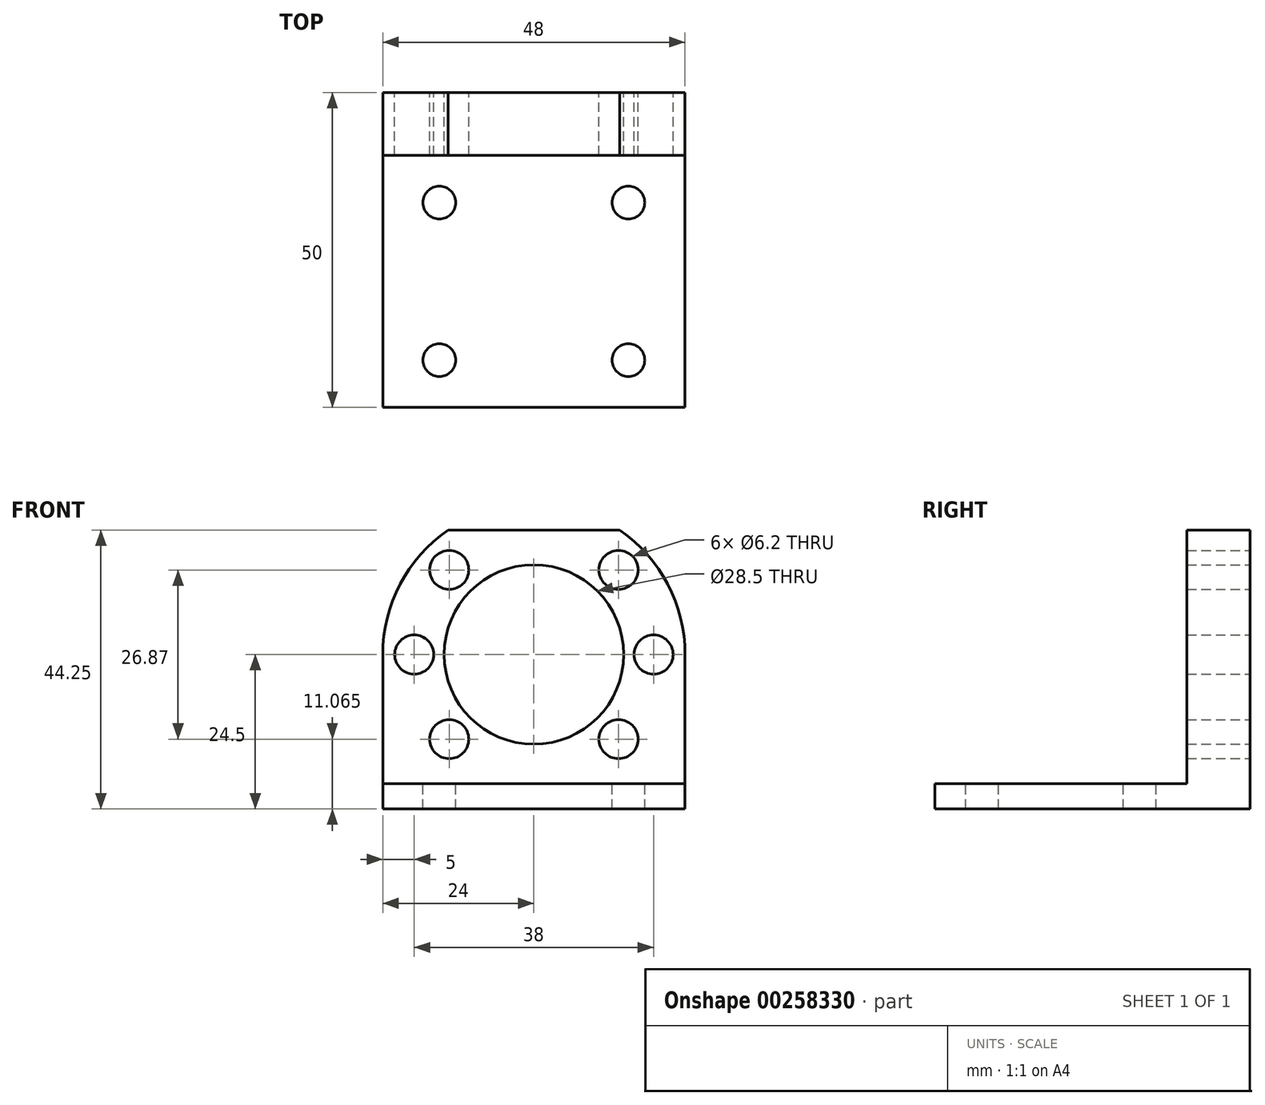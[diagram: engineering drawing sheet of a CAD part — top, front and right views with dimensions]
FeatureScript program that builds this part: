
annotation { "Feature Type Name" : "Feature", "Feature Type Description" : "" }
export const myFeature = defineFeature(function(context is Context, id is Id, definition is map)
    precondition{}
    {
        {
            var Q0;
            Q0=qCreatedBy(makeId("Front.planeOp"),FACE);
            var sketch = newSketch(context, id + "F0", { "sketchPlane" : qUnion([Q0])});
            skCircle(sketch, "E0", {"center": v(0, 0) * mm, "radius": 14.25 * mm});
            skArc(sketch, "E1", {"start": v(-13.64, 19.75) * mm, "mid": v(-21.25, 11.15) * mm, "end": v(-24, 0) * mm});
            skLineSegment(sketch, "E2", {"start": v(-13.64, 19.75) * mm, "end": v(13.64, 19.75) * mm});
            skLineSegment(sketch, "E3", {"start": v(24, 0) * mm, "end": v(-24, 0) * mm, "construction": true});
            skCircle(sketch, "E4", {"center": v(0, 0) * mm, "radius": 19 * mm, "construction": true});
            skCircle(sketch, "E5", {"center": v(-13.44, 13.44) * mm, "radius": 3.1 * mm});
            skCircle(sketch, "E6", {"center": v(-19, 0) * mm, "radius": 3.1 * mm});
            skCircle(sketch, "E7", {"center": v(-13.44, -13.44) * mm, "radius": 3.1 * mm});
            skCircle(sketch, "E8", {"center": v(13.44, -13.44) * mm, "radius": 3.1 * mm});
            skCircle(sketch, "E9", {"center": v(19, 0) * mm, "radius": 3.1 * mm});
            skCircle(sketch, "E10", {"center": v(13.44, 13.44) * mm, "radius": 3.1 * mm});
            skLineSegment(sketch, "E11", {"start": v(0, 24) * mm, "end": v(0, -24) * mm, "construction": true});
            skLineSegment(sketch, "E12", {"start": v(-16.97, 16.97) * mm, "end": v(16.97, -16.97) * mm, "construction": true});
            skLineSegment(sketch, "E13", {"start": v(-24, 0) * mm, "end": v(-24, -24.5) * mm});
            skLineSegment(sketch, "E14", {"start": v(24, 0) * mm, "end": v(24, -24.5) * mm});
            skLineSegment(sketch, "E15", {"start": v(24, -24.5) * mm, "end": v(-24, -24.5) * mm});
            skArc(sketch, "E16.trimOffspring", {"start": v(24, 0) * mm, "mid": v(21.25, 11.15) * mm, "end": v(13.64, 19.75) * mm});
            skCircle(sketch, "E17", {"center": v(0, 0) * mm, "radius": 24 * mm, "construction": true});
            skSolve(sketch);
        }
        {
            var Q0;
            Q0=qSketchRegion(id+"F0",true);
            extrude(context, id + "F1", {"entities" : qUnion([Q0]), "depth" : 10 * mm});
        }
        {
            var Q0;
            Q0=makeQuery(id+"F1.opExtrude","CAP_FACE",FACE,{"disambiguationData":[OSD([sQuery(id+"F0.wireOp",EDGE,"E0"),sQuery(id+"F0.wireOp",EDGE,"E1"),sQuery(id+"F0.wireOp",EDGE,"E2"),sQuery(id+"F0.wireOp",EDGE,"E5"),sQuery(id+"F0.wireOp",EDGE,"E6"),sQuery(id+"F0.wireOp",EDGE,"E7"),sQuery(id+"F0.wireOp",EDGE,"E8"),sQuery(id+"F0.wireOp",EDGE,"E9"),sQuery(id+"F0.wireOp",EDGE,"E10"),sQuery(id+"F0.wireOp",EDGE,"E13"),sQuery(id+"F0.wireOp",EDGE,"E14"),sQuery(id+"F0.wireOp",EDGE,"E15"),sQuery(id+"F0.wireOp",EDGE,"E16.trimOffspring")])],"isStart":false});
            var sketch = newSketch(context, id + "F2", { "sketchPlane" : qUnion([Q0])});
            skLineSegment(sketch, "E18.bottom", {"start": v(-24, -24.5) * mm, "end": v(24, -24.5) * mm});
            skLineSegment(sketch, "E18.top", {"start": v(-24, -20.5) * mm, "end": v(24, -20.5) * mm});
            skLineSegment(sketch, "E18.left", {"start": v(-24, -24.5) * mm, "end": v(-24, -20.5) * mm});
            skLineSegment(sketch, "E18.right", {"start": v(24, -24.5) * mm, "end": v(24, -20.5) * mm});
            skSolve(sketch);
        }
        {
            var Q0;
            Q0=qSketchRegion(id+"F2",true);
            extrude(context, id + "F3", {"entities" : qUnion([Q0]), "operationType" : NewBodyOperationType.ADD, "depth" : 40 * mm});
        }
        {
            var Q0;
            Q0=makeQuery(id+"F3.opExtrude","SWEPT_FACE",FACE,{"disambiguationData":[OSD([sQuery(id+"F2.wireOp",EDGE,"E18.top")])]});
            var sketch = newSketch(context, id + "F4", { "sketchPlane" : qUnion([Q0])});
            skLineSegment(sketch, "E19", {"start": v(-24, -10) * mm, "end": v(24, -50) * mm, "construction": true});
            skLineSegment(sketch, "E20", {"start": v(24, -10) * mm, "end": v(-24, -50) * mm, "construction": true});
            skCircle(sketch, "E21", {"center": v(-15, -17.5) * mm, "radius": 2.6 * mm});
            skCircle(sketch, "E22", {"center": v(-15, -42.5) * mm, "radius": 2.6 * mm});
            skCircle(sketch, "E23", {"center": v(15, -42.5) * mm, "radius": 2.6 * mm});
            skCircle(sketch, "E24", {"center": v(15, -17.5) * mm, "radius": 2.6 * mm});
            skLineSegment(sketch, "E25", {"start": v(0, -10) * mm, "end": v(0, -50) * mm, "construction": true});
            skLineSegment(sketch, "E26", {"start": v(24, -30) * mm, "end": v(-24, -30) * mm, "construction": true});
            skSolve(sketch);
        }
        {
            var Q0;
            Q0=qSketchRegion(id+"F4",true);
            extrude(context, id + "F5", {"entities" : qUnion([Q0]), "operationType" : NewBodyOperationType.REMOVE, "endBound" : BoundingType.UP_TO_NEXT, "oppositeDirection" : true, "depth" : 25 * mm});
        }
    });
